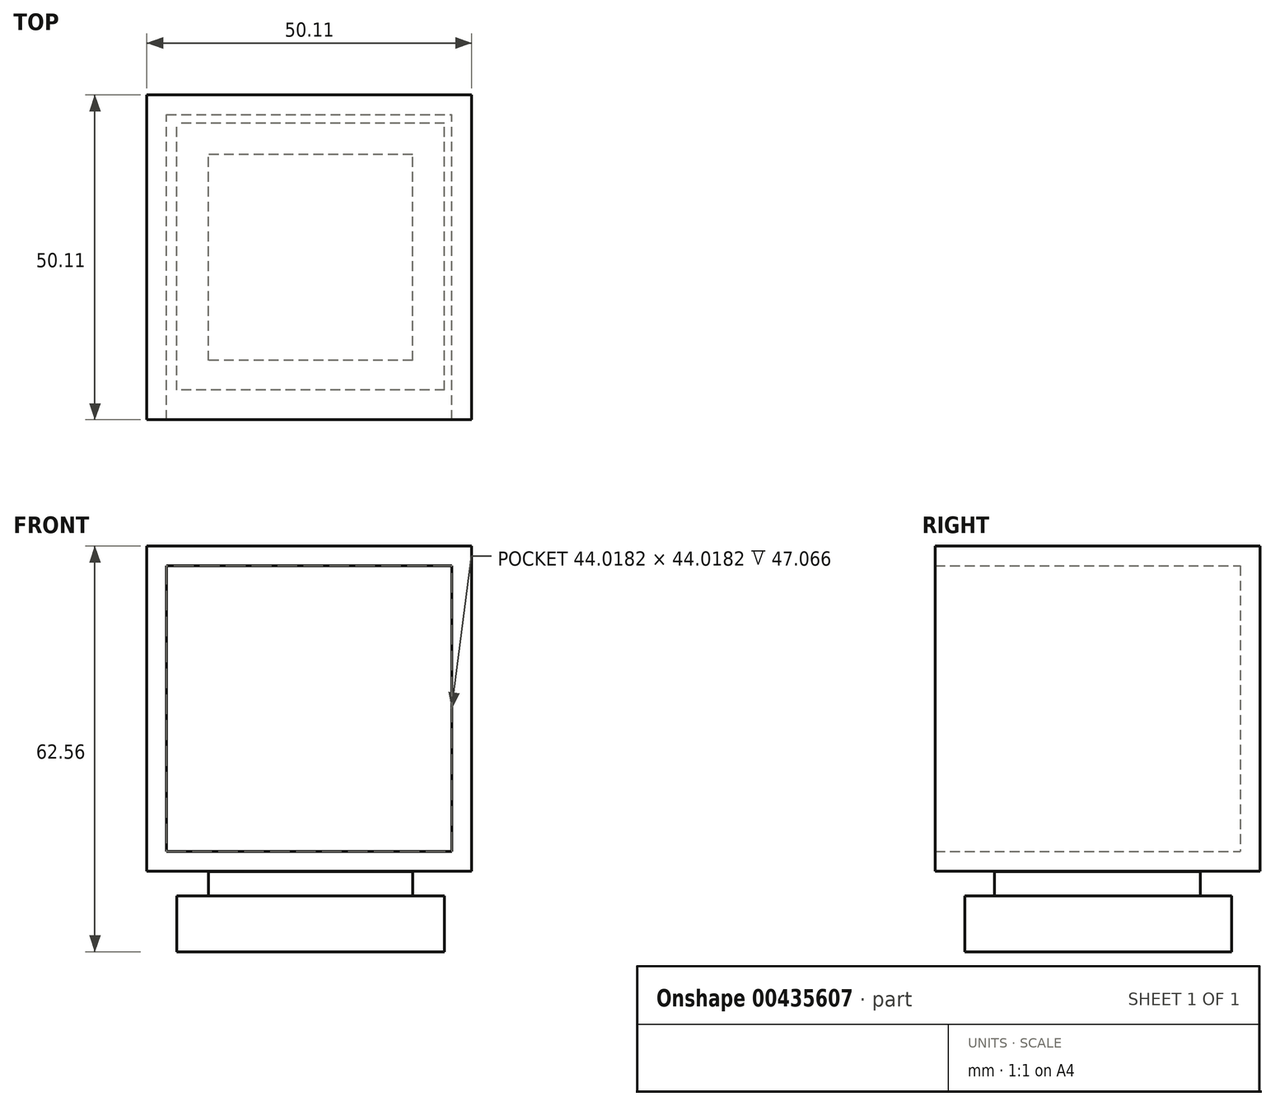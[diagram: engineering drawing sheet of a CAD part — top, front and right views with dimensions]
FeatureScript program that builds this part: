
annotation { "Feature Type Name" : "Feature", "Feature Type Description" : "" }
export const myFeature = defineFeature(function(context is Context, id is Id, definition is map)
    precondition{}
    {
        {
            var Q0;
            Q0=qCreatedBy(makeId("Front.planeOp"),FACE);
            var sketch = newSketch(context, id + "F0", { "sketchPlane" : qUnion([Q0])});
            skLineSegment(sketch, "E0.bottom", {"start": v(-25.25, 30.62) * mm, "end": v(24.86, 30.62) * mm});
            skLineSegment(sketch, "E0.top", {"start": v(-25.25, -19.5) * mm, "end": v(24.86, -19.5) * mm});
            skLineSegment(sketch, "E0.left", {"start": v(-25.25, 30.62) * mm, "end": v(-25.25, -19.5) * mm});
            skLineSegment(sketch, "E0.right", {"start": v(24.86, 30.62) * mm, "end": v(24.86, -19.5) * mm});
            skSolve(sketch);
        }
        {
            var Q0;
            Q0 = qSketchRegion(id + "F0", true);
            var Q1;
            Q1=makeQuery(id+"F0.imprint","IMPRINT",FACE,{"disambiguationData":[TD([[makeQuery(id+"F0.imprint","IMPRINT",EDGE,{"derivedFrom":sQuery(id+"F0.wireOp",EDGE,"E0.bottom")}),-1.0]])]});
            extrude(context, id + "F1", {"entities" : qUnion([Q0, Q1]), "depth" : 50.1 * mm});
        }
        {
            var Q0;
            Q0=makeQuery(id+"F1.opExtrude","CAP_FACE",FACE,{"disambiguationData":[OSD([sQuery(id+"F0.wireOp",EDGE,"E0.bottom"),sQuery(id+"F0.wireOp",EDGE,"E0.top"),sQuery(id+"F0.wireOp",EDGE,"E0.left"),sQuery(id+"F0.wireOp",EDGE,"E0.right")])],"isStart":false});
            shell(context, id + "F2", {"entities" : qUnion([Q0]), "thickness" : 3.05 * mm});
        }
        {
            var Q0;
            Q0=qCreatedBy(makeId("Right.planeOp"),FACE);
            var sketch = newSketch(context, id + "F3", { "sketchPlane" : qUnion([Q0])});
            skLineSegment(sketch, "E1.bottom", {"start": v(-40.97, -19.58) * mm, "end": v(-9.22, -19.58) * mm});
            skLineSegment(sketch, "E1.top", {"start": v(-40.97, -23.3) * mm, "end": v(-9.22, -23.3) * mm});
            skLineSegment(sketch, "E1.left", {"start": v(-40.97, -19.58) * mm, "end": v(-40.97, -23.3) * mm});
            skLineSegment(sketch, "E1.right", {"start": v(-9.22, -19.58) * mm, "end": v(-9.22, -23.3) * mm});
            skLineSegment(sketch, "E2.bottom", {"start": v(-45.54, -23.3) * mm, "end": v(-4.4, -23.3) * mm});
            skLineSegment(sketch, "E2.top", {"start": v(-45.54, -31.94) * mm, "end": v(-4.4, -31.94) * mm});
            skLineSegment(sketch, "E2.left", {"start": v(-45.54, -23.3) * mm, "end": v(-45.54, -31.94) * mm});
            skLineSegment(sketch, "E2.right", {"start": v(-4.4, -23.3) * mm, "end": v(-4.4, -31.94) * mm});
            skSolve(sketch);
        }
        {
            var Q0;
            Q0=makeQuery(id+"F3.imprint","IMPRINT",FACE,{"disambiguationData":[TD([[makeQuery(id+"F3.imprint","IMPRINT",EDGE,{"derivedFrom":sQuery(id+"F3.wireOp",EDGE,"E1.bottom")}),-1.0]])]});
            extrude(context, id + "F4", {"entities" : qUnion([Q0]), "depth" : 31.5 * mm, "symmetric" : true});
        }
        {
            var Q0;
            {var subQ1=sQuery(id+"F3.wireOp",EDGE,"E1.top");Q0=makeQuery(id+"F3.imprint","IMPRINT",FACE,{"disambiguationData":[TD([[makeQuery(id+"F3.imprint","IMPRINT",EDGE,{"derivedFrom":subQ1}),-1.0]])]});}
            extrude(context, id + "F5", {"entities" : qUnion([Q0]), "operationType" : NewBodyOperationType.ADD, "depth" : 41.33 * mm, "symmetric" : true});
        }
    });
